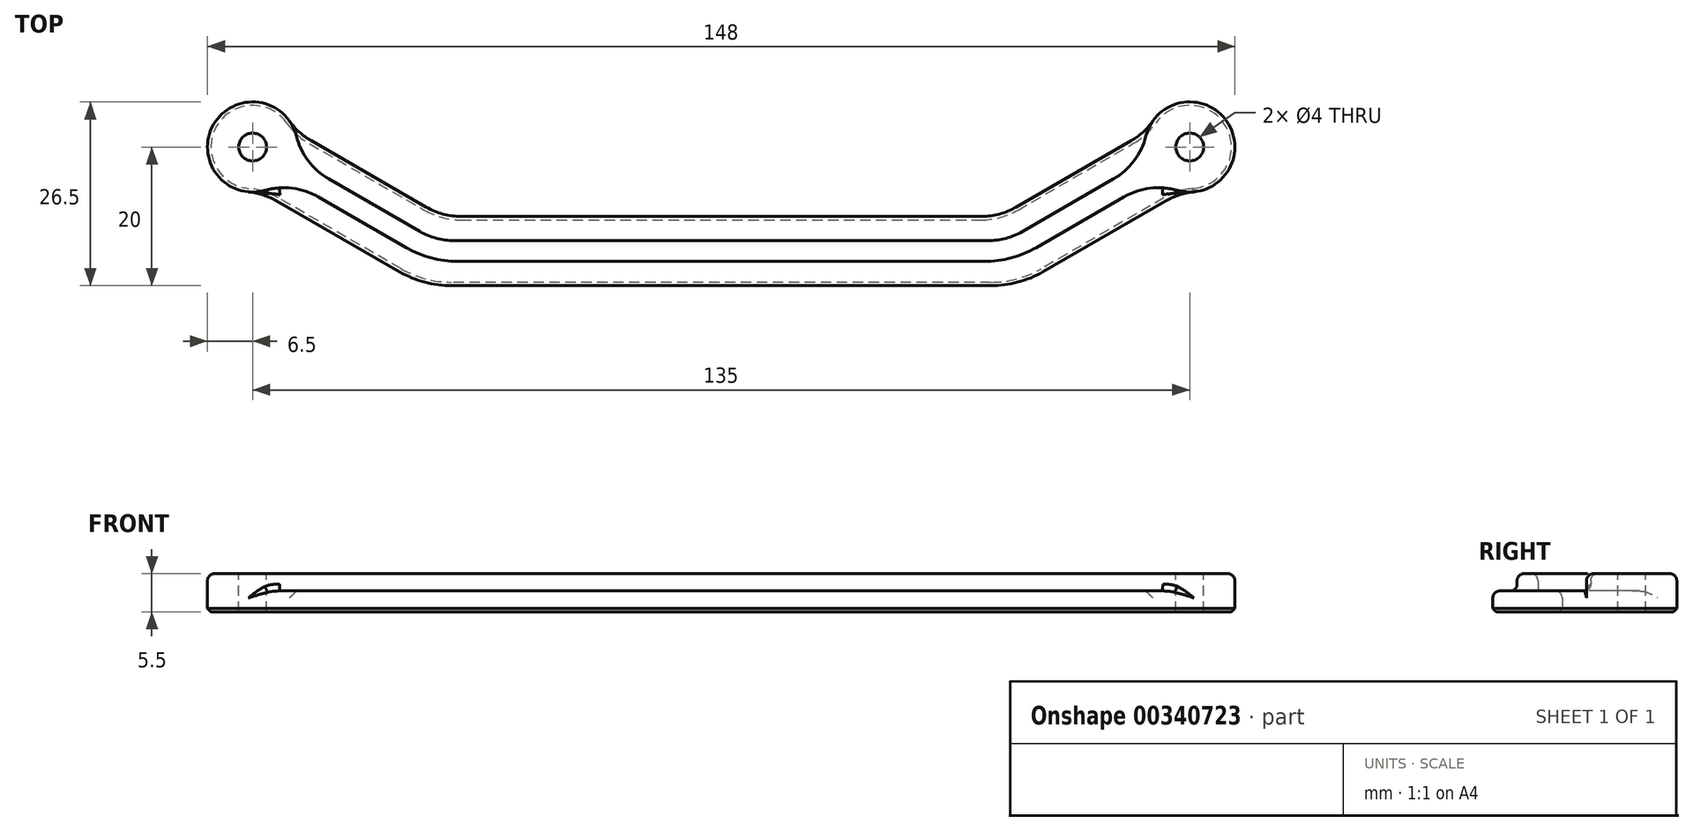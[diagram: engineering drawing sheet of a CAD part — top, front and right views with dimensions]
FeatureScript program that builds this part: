
annotation { "Feature Type Name" : "Feature", "Feature Type Description" : "" }
export const myFeature = defineFeature(function(context is Context, id is Id, definition is map)
    precondition{}
    {
        {
            var Q0;
            Q0=qCreatedBy(makeId("Top.planeOp"),FACE);
            var sketch = newSketch(context, id + "F0", { "sketchPlane" : qUnion([Q0])});
            skLineSegment(sketch, "E0", {"start": v(0, 0) * mm, "end": v(67.5, 0) * mm, "construction": true});
            skLineSegment(sketch, "E1", {"start": v(0, 0) * mm, "end": v(0, 13.51) * mm, "construction": true});
            skCircle(sketch, "E2", {"center": v(67.5, 0) * mm, "radius": 6.5 * mm});
            skCircle(sketch, "E3.MirrorC", {"center": v(-67.5, 0) * mm, "radius": 6.5 * mm});
            skSolve(sketch);
        }
        {
            var Q0;
            Q0=qSketchRegion(id+"F0",true);
            extrude(context, id + "F1", {"entities" : qUnion([Q0]), "depth" : 5.5 * mm});
        }
        {
            var Q0;
            Q0=qCreatedBy(makeId("Top.planeOp"),FACE);
            var sketch = newSketch(context, id + "F2", { "sketchPlane" : qUnion([Q0])});
            skLineSegment(sketch, "E4", {"start": v(-67.5, 0) * mm, "end": v(67.5, 0) * mm, "construction": true});
            skLineSegment(sketch, "E5", {"start": v(-67.5, 0) * mm, "end": v(-41.52, -15) * mm, "construction": true});
            skLineSegment(sketch, "E6", {"start": v(-41.52, -15) * mm, "end": v(0, -15) * mm, "construction": true});
            skLineSegment(sketch, "E7", {"start": v(0, -15) * mm, "end": v(0, 0) * mm, "construction": true});
            skLineSegment(sketch, "E8.MirrorCS", {"start": v(41.52, -15) * mm, "end": v(0, -15) * mm, "construction": true});
            skLineSegment(sketch, "E9.MirrorCS", {"start": v(67.5, 0) * mm, "end": v(41.52, -15) * mm, "construction": true});
            skLineSegment(sketch, "E10.0", {"start": v(70, -4.33) * mm, "end": v(42.86, -20) * mm});
            skLineSegment(sketch, "E10.1", {"start": v(42.86, -20) * mm, "end": v(0, -20) * mm});
            skLineSegment(sketch, "E10.2", {"start": v(-42.86, -20) * mm, "end": v(0, -20) * mm});
            skLineSegment(sketch, "E10.3", {"start": v(-70, -4.33) * mm, "end": v(-42.86, -20) * mm});
            skLineSegment(sketch, "E11.0", {"start": v(65, 4.33) * mm, "end": v(40.18, -10) * mm});
            skLineSegment(sketch, "E11.1", {"start": v(40.18, -10) * mm, "end": v(0, -10) * mm});
            skLineSegment(sketch, "E11.2", {"start": v(-40.18, -10) * mm, "end": v(0, -10) * mm});
            skLineSegment(sketch, "E11.3", {"start": v(-65, 4.33) * mm, "end": v(-40.18, -10) * mm});
            skLineSegment(sketch, "E12", {"start": v(-70, -4.33) * mm, "end": v(-65, 4.33) * mm});
            skLineSegment(sketch, "E13", {"start": v(65, 4.33) * mm, "end": v(70, -4.33) * mm});
            skSolve(sketch);
        }
        {
            var Q0;
            Q0=qSketchRegion(id+"F2",true);
            extrude(context, id + "F3", {"entities" : qUnion([Q0]), "operationType" : NewBodyOperationType.ADD, "depth" : 3 * mm});
        }
        {
            var Q0;
            Q0=makeQuery(id+"F3.opExtrude","CAP_FACE",FACE,{"disambiguationData":[OSD([sQuery(id+"F2.wireOp",EDGE,"E10.0"),sQuery(id+"F2.wireOp",EDGE,"E10.1"),sQuery(id+"F2.wireOp",EDGE,"E10.2"),sQuery(id+"F2.wireOp",EDGE,"E10.3"),sQuery(id+"F2.wireOp",EDGE,"E11.0"),sQuery(id+"F2.wireOp",EDGE,"E11.1"),sQuery(id+"F2.wireOp",EDGE,"E11.2"),sQuery(id+"F2.wireOp",EDGE,"E11.3"),sQuery(id+"F2.wireOp",EDGE,"E12"),sQuery(id+"F2.wireOp",EDGE,"E13")])],"isStart":false});
            var sketch = newSketch(context, id + "F4", { "sketchPlane" : qUnion([Q0])});
            skLineSegment(sketch, "E14.0", {"start": v(68.25, -1.3) * mm, "end": v(41.92, -16.5) * mm});
            skLineSegment(sketch, "E14.1", {"start": v(41.92, -16.5) * mm, "end": v(0, -16.5) * mm});
            skLineSegment(sketch, "E14.2", {"start": v(-41.92, -16.5) * mm, "end": v(0, -16.5) * mm});
            skLineSegment(sketch, "E14.3", {"start": v(-68.25, -1.3) * mm, "end": v(-41.92, -16.5) * mm});
            skLineSegment(sketch, "E15.0", {"start": v(66.75, 1.3) * mm, "end": v(41.12, -13.5) * mm});
            skLineSegment(sketch, "E15.1", {"start": v(41.12, -13.5) * mm, "end": v(0, -13.5) * mm});
            skLineSegment(sketch, "E15.2", {"start": v(-41.12, -13.5) * mm, "end": v(0, -13.5) * mm});
            skLineSegment(sketch, "E15.3", {"start": v(-66.75, 1.3) * mm, "end": v(-41.12, -13.5) * mm});
            skLineSegment(sketch, "E16", {"start": v(-68.25, -1.3) * mm, "end": v(-66.75, 1.3) * mm});
            skLineSegment(sketch, "E17", {"start": v(66.75, 1.3) * mm, "end": v(68.25, -1.3) * mm});
            skSolve(sketch);
        }
        {
            var Q0;
            Q0=qSketchRegion(id+"F4",true);
            var Q1;
            Q1=makeQuery(id+"F1.opExtrude","CAP_FACE",FACE,{"disambiguationData":[OSD([sQuery(id+"F0.wireOp",EDGE,"E3.MirrorC")])],"isStart":false});
            extrude(context, id + "F5", {"entities" : qUnion([Q0]), "operationType" : NewBodyOperationType.ADD, "endBound" : BoundingType.UP_TO_SURFACE, "endBoundEntityFace" : qUnion([Q1]), "depth" : 25 * mm});
        }
        {
            var Q0;
            {var subQ0=sQuery(id+"F0.wireOp",EDGE,"E3.MirrorC");Q0=makeQuery(id+"F5.boolean.opBoolean","MERGE",FACE,{"derivedFrom":[makeQuery(id+"F1.opExtrude","CAP_FACE",FACE,{"disambiguationData":[OSD([sQuery(id+"F0.wireOp",EDGE,"E2")])],"isStart":false}),makeQuery(id+"F1.opExtrude","CAP_FACE",FACE,{"disambiguationData":[OSD([subQ0])],"isStart":false}),makeQuery(id+"F5.opExtrude","CAP_FACE",FACE,{"disambiguationData":[OSD([subQ0])],"isStart":false})]});}
            var sketch = newSketch(context, id + "F6", { "sketchPlane" : qUnion([Q0])});
            skCircle(sketch, "E18", {"center": v(-67.5, 0) * mm, "radius": 2 * mm});
            skCircle(sketch, "E19", {"center": v(67.5, 0) * mm, "radius": 2 * mm});
            skSolve(sketch);
        }
        {
            var Q0;
            Q0=qSketchRegion(id+"F6",true);
            extrude(context, id + "F7", {"entities" : qUnion([Q0]), "operationType" : NewBodyOperationType.REMOVE, "endBound" : BoundingType.THROUGH_ALL, "oppositeDirection" : true, "depth" : 25 * mm});
        }
        {
            var Q0;
            Q0=makeQuery(id+"F3.boolean.opBoolean","INTERSECT",EDGE,{"derivedFrom":[makeQuery(id+"F1.opExtrude","SWEPT_FACE",FACE,{"disambiguationData":[OSD([sQuery(id+"F0.wireOp",EDGE,"E3.MirrorC")])]}),makeQuery(id+"F3.opExtrude","SWEPT_FACE",FACE,{"disambiguationData":[OSD([sQuery(id+"F2.wireOp",EDGE,"E10.3")])]})]});
            var Q1;
            Q1=makeQuery(id+"F3.boolean.opBoolean","INTERSECT",EDGE,{"derivedFrom":[makeQuery(id+"F1.opExtrude","SWEPT_FACE",FACE,{"disambiguationData":[OSD([sQuery(id+"F0.wireOp",EDGE,"E2")])]}),makeQuery(id+"F3.opExtrude","SWEPT_FACE",FACE,{"disambiguationData":[OSD([sQuery(id+"F2.wireOp",EDGE,"E10.0")])]})]});
            var Q2;
            Q2=makeQuery(id+"F3.boolean.opBoolean","INTERSECT",EDGE,{"derivedFrom":[makeQuery(id+"F1.opExtrude","SWEPT_FACE",FACE,{"disambiguationData":[OSD([sQuery(id+"F0.wireOp",EDGE,"E3.MirrorC")])]}),makeQuery(id+"F3.opExtrude","SWEPT_FACE",FACE,{"disambiguationData":[OSD([sQuery(id+"F2.wireOp",EDGE,"E11.3")])]})]});
            var Q3;
            Q3=makeQuery(id+"F3.boolean.opBoolean","INTERSECT",EDGE,{"derivedFrom":[makeQuery(id+"F1.opExtrude","SWEPT_FACE",FACE,{"disambiguationData":[OSD([sQuery(id+"F0.wireOp",EDGE,"E2")])]}),makeQuery(id+"F3.opExtrude","SWEPT_FACE",FACE,{"disambiguationData":[OSD([sQuery(id+"F2.wireOp",EDGE,"E11.0")])]})]});
            fillet(context, id + "F8", {"entities" : qUnion([Q0, Q1, Q2, Q3]), "radius" : 10 * mm, "tangentPropagation" : true, "allowEdgeOverflow" : false});
        }
        {
            var Q0;
            Q0=makeQuery(id+"F5.boolean.opBoolean","INTERSECT",EDGE,{"derivedFrom":[makeQuery(id+"F1.opExtrude","SWEPT_FACE",FACE,{"disambiguationData":[OSD([sQuery(id+"F0.wireOp",EDGE,"E2")])]}),makeQuery(id+"F5.opExtrude","SWEPT_FACE",FACE,{"disambiguationData":[OSD([sQuery(id+"F4.wireOp",EDGE,"E15.0")])]})]});
            var Q1;
            Q1=makeQuery(id+"F3.opExtrude","SWEPT_EDGE",EDGE,{"disambiguationData":[OSD([sQuery(id+"F2.wireOp",EDGE,"E11.0"),sQuery(id+"F2.wireOp",EDGE,"E11.1")])]});
            var Q2;
            Q2=makeQuery(id+"F5.opExtrude","SWEPT_EDGE",EDGE,{"disambiguationData":[OSD([sQuery(id+"F4.wireOp",EDGE,"E15.0"),sQuery(id+"F4.wireOp",EDGE,"E15.1")])]});
            var Q3;
            Q3=makeQuery(id+"F5.opExtrude","SWEPT_EDGE",EDGE,{"disambiguationData":[OSD([sQuery(id+"F4.wireOp",EDGE,"E15.2"),sQuery(id+"F4.wireOp",EDGE,"E15.3")])]});
            var Q4;
            Q4=makeQuery(id+"F3.opExtrude","SWEPT_EDGE",EDGE,{"disambiguationData":[OSD([sQuery(id+"F2.wireOp",EDGE,"E11.2"),sQuery(id+"F2.wireOp",EDGE,"E11.3")])]});
            var Q5;
            Q5=makeQuery(id+"F5.boolean.opBoolean","INTERSECT",EDGE,{"derivedFrom":[makeQuery(id+"F1.opExtrude","SWEPT_FACE",FACE,{"disambiguationData":[OSD([sQuery(id+"F0.wireOp",EDGE,"E3.MirrorC")])]}),makeQuery(id+"F5.opExtrude","SWEPT_FACE",FACE,{"disambiguationData":[OSD([sQuery(id+"F4.wireOp",EDGE,"E15.3")])]})]});
            var Q6;
            Q6=makeQuery(id+"F5.boolean.opBoolean","INTERSECT",EDGE,{"derivedFrom":[makeQuery(id+"F1.opExtrude","SWEPT_FACE",FACE,{"disambiguationData":[OSD([sQuery(id+"F0.wireOp",EDGE,"E3.MirrorC")])]}),makeQuery(id+"F5.opExtrude","SWEPT_FACE",FACE,{"disambiguationData":[OSD([sQuery(id+"F4.wireOp",EDGE,"E14.3")])]})]});
            var Q7;
            Q7=makeQuery(id+"F5.boolean.opBoolean","INTERSECT",EDGE,{"derivedFrom":[makeQuery(id+"F1.opExtrude","SWEPT_FACE",FACE,{"disambiguationData":[OSD([sQuery(id+"F0.wireOp",EDGE,"E2")])]}),makeQuery(id+"F5.opExtrude","SWEPT_FACE",FACE,{"disambiguationData":[OSD([sQuery(id+"F4.wireOp",EDGE,"E14.0")])]})]});
            fillet(context, id + "F9", {"entities" : qUnion([Q0, Q1, Q2, Q3, Q4, Q5, Q6, Q7]), "radius" : 10 * mm, "tangentPropagation" : true, "allowEdgeOverflow" : false});
        }
        {
            var Q0;
            Q0=makeQuery(id+"F3.opExtrude","SWEPT_EDGE",EDGE,{"disambiguationData":[OSD([sQuery(id+"F2.wireOp",EDGE,"E10.0"),sQuery(id+"F2.wireOp",EDGE,"E10.1")])]});
            var Q1;
            Q1=makeQuery(id+"F5.opExtrude","SWEPT_EDGE",EDGE,{"disambiguationData":[OSD([sQuery(id+"F4.wireOp",EDGE,"E14.0"),sQuery(id+"F4.wireOp",EDGE,"E14.1")])]});
            var Q2;
            Q2=makeQuery(id+"F3.opExtrude","SWEPT_EDGE",EDGE,{"disambiguationData":[OSD([sQuery(id+"F2.wireOp",EDGE,"E10.2"),sQuery(id+"F2.wireOp",EDGE,"E10.3")])]});
            var Q3;
            Q3=makeQuery(id+"F5.opExtrude","SWEPT_EDGE",EDGE,{"disambiguationData":[OSD([sQuery(id+"F4.wireOp",EDGE,"E14.2"),sQuery(id+"F4.wireOp",EDGE,"E14.3")])]});
            fillet(context, id + "F10", {"entities" : qUnion([Q0, Q1, Q2, Q3]), "radius" : 15 * mm, "tangentPropagation" : true, "allowEdgeOverflow" : false});
        }
        {
            var Q0;
            Q0=makeQuery(id+"F3.opExtrude","CAP_EDGE",EDGE,{"disambiguationData":[OSD([sQuery(id+"F2.wireOp",EDGE,"E10.1"),sQuery(id+"F2.wireOp",EDGE,"E10.2")])],"isStart":false});
            var Q1;
            {var subQ0=sQuery(id+"F0.wireOp",EDGE,"E3.MirrorC");Q1=makeQuery(id+"F10.opFillet","BLEND_EDGE",EDGE,{"blendedFrom":[makeQuery(id+"F5.opExtrude","SWEPT_EDGE",EDGE,{"disambiguationData":[OSD([sQuery(id+"F4.wireOp",EDGE,"E14.2"),sQuery(id+"F4.wireOp",EDGE,"E14.3")])]}),makeQuery(id+"F5.boolean.opBoolean","MERGE",FACE,{"derivedFrom":[makeQuery(id+"F1.opExtrude","CAP_FACE",FACE,{"disambiguationData":[OSD([sQuery(id+"F0.wireOp",EDGE,"E2")])],"isStart":false}),makeQuery(id+"F1.opExtrude","CAP_FACE",FACE,{"disambiguationData":[OSD([subQ0])],"isStart":false}),makeQuery(id+"F5.opExtrude","CAP_FACE",FACE,{"disambiguationData":[OSD([subQ0])],"isStart":false})]})],"blendedInto":[makeQuery(id+"F5.boolean.opBoolean","MERGE",FACE,{"derivedFrom":[makeQuery(id+"F1.opExtrude","CAP_FACE",FACE,{"disambiguationData":[OSD([sQuery(id+"F0.wireOp",EDGE,"E2")])],"isStart":false}),makeQuery(id+"F1.opExtrude","CAP_FACE",FACE,{"disambiguationData":[OSD([subQ0])],"isStart":false}),makeQuery(id+"F5.opExtrude","CAP_FACE",FACE,{"disambiguationData":[OSD([subQ0])],"isStart":false})]})]});}
            var Q2;
            Q2=makeQuery(id+"F3.opExtrude","CAP_EDGE",EDGE,{"disambiguationData":[OSD([sQuery(id+"F2.wireOp",EDGE,"E11.3")])],"isStart":false});
            fillet(context, id + "F11", {"entities" : qUnion([Q0, Q1, Q2]), "radius" : 1 * mm, "tangentPropagation" : true, "allowEdgeOverflow" : false});
        }
        {
            var Q0;
            Q0=makeQuery(id+"F3.opExtrude","CAP_EDGE",EDGE,{"disambiguationData":[OSD([sQuery(id+"F2.wireOp",EDGE,"E11.1"),sQuery(id+"F2.wireOp",EDGE,"E11.2")])],"isStart":true});
            chamfer(context, id + "F12", {"entities" : qUnion([Q0]), "width" : .5 * mm, "tangentPropagation" : true});
        }
        {
            var Q0;
            Q0=makeQuery(id+"F5.opExtrude","CAP_EDGE",EDGE,{"disambiguationData":[OSD([sQuery(id+"F4.wireOp",EDGE,"E15.1"),sQuery(id+"F4.wireOp",EDGE,"E15.2")])],"isStart":true});
            var Q1;
            Q1=makeQuery(id+"F5.opExtrude","CAP_EDGE",EDGE,{"disambiguationData":[OSD([sQuery(id+"F4.wireOp",EDGE,"E14.1"),sQuery(id+"F4.wireOp",EDGE,"E14.2")])],"isStart":true});
            fillet(context, id + "F13", {"entities" : qUnion([Q0, Q1]), "radius" : 1 * mm, "tangentPropagation" : true, "allowEdgeOverflow" : false});
        }
    });
